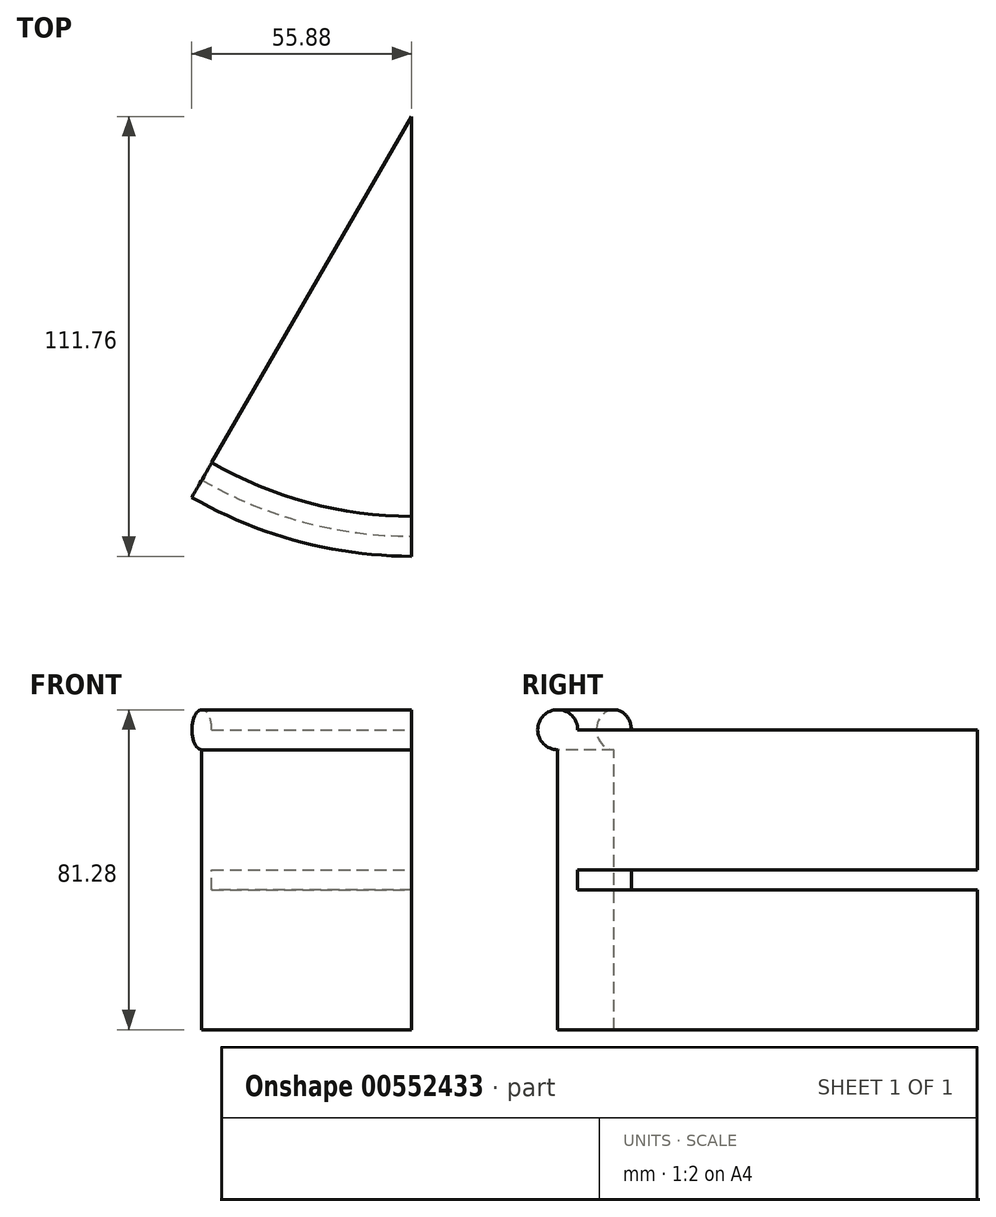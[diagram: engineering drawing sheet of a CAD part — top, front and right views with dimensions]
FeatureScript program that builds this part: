
annotation { "Feature Type Name" : "Feature", "Feature Type Description" : "" }
export const myFeature = defineFeature(function(context is Context, id is Id, definition is map)
    precondition{}
    {
        {
            var Q0;
            Q0=qCreatedBy(makeId("Right.planeOp"),FACE);
            var sketch = newSketch(context, id + "F0", { "sketchPlane" : qUnion([Q0])});
            skLineSegment(sketch, "E0.bottom", {"start": v(0, 0) * mm, "end": v(-101.6, 0) * mm});
            skLineSegment(sketch, "E0.top", {"start": v(0, 35.56) * mm, "end": v(-101.6, 35.56) * mm});
            skLineSegment(sketch, "E0.left", {"start": v(0, 0) * mm, "end": v(0, 35.56) * mm});
            skLineSegment(sketch, "E0.right", {"start": v(-101.6, 0) * mm, "end": v(-101.6, 35.56) * mm});
            skLineSegment(sketch, "E1.bottom", {"start": v(-101.6, 0) * mm, "end": v(-106.68, 0) * mm});
            skLineSegment(sketch, "E1.top", {"start": v(-101.6, 76.2) * mm, "end": v(-106.68, 76.2) * mm});
            skLineSegment(sketch, "E1.left", {"start": v(-101.6, 0) * mm, "end": v(-101.6, 76.2) * mm});
            skLineSegment(sketch, "E1.right", {"start": v(-106.68, 0) * mm, "end": v(-106.68, 76.2) * mm});
            skLineSegment(sketch, "E2.bottom", {"start": v(-101.6, 76.2) * mm, "end": v(0, 76.2) * mm});
            skLineSegment(sketch, "E2.top", {"start": v(-101.6, 40.64) * mm, "end": v(0, 40.64) * mm});
            skLineSegment(sketch, "E2.left", {"start": v(-101.6, 76.2) * mm, "end": v(-101.6, 40.64) * mm});
            skLineSegment(sketch, "E2.right", {"start": v(0, 76.2) * mm, "end": v(0, 40.64) * mm});
            skCircle(sketch, "E3", {"center": v(-106.68, 76.2) * mm, "radius": 5.08 * mm});
            skSolve(sketch);
        }
        {
            var Q0;
            Q0 = qSketchRegion(id + "F0", true);
            var Q1;
            Q1=sQuery(id+"F0.wireOp",EDGE,"E2.right");
            revolve(context, id + "F1", {"entities" : qUnion([Q0]), "axis" : qUnion([Q1]), "revolveType" : RevolveType.ONE_DIRECTION, "angle" : 30 * degree});
        }
    });
